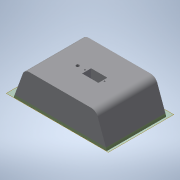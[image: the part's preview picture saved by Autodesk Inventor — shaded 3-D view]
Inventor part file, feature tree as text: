
AUTODESK INVENTOR PART (.ipt)
format: ipt  version: 2020 (Build 240168000, 168)  size: 355,328 bytes
history: native  units: mm
features: extrude x13, sketch x10, other x7, reference x6, projected_geometry x4, fillet x1, hole x1
ambient origin geometry x8: Origin, YZ Plane, XZ Plane, XY Plane, X Axis, Y Axis, Z Axis, Center Point
bodies: Body1 (feature_tree)
feature tree (42):
  other  "Bryła1"
  sketch  "Szkic1"
  other  "Płaszczyzna konstrukcyjna1"
  extrude  "Wyciągnięcie proste1"  Depth=3.0mm
  sketch  "Szkic2"
  other  "Płaszczyzna konstrukcyjna2"
  extrude  "Wyciągnięcie proste2"  Depth=3.0mm
  extrude  "Wyciągnięcie proste3"  Depth=3.0mm
  extrude  "Wyciągnięcie proste4"  Depth=40.0mm
  extrude  "Wyciągnięcie proste5"  Depth=12.217305mm
  extrude  "Wyciągnięcie proste6"  Depth=12.217305mm
  fillet  "Zaokrąglenie1"  Radius=75.0mm
  extrude  "Wyciągnięcie proste7"  Depth=3.0mm TaperAngle=0.0deg
  extrude  "Wyciągnięcie proste8"  Depth=83.0mm TaperAngle=0.0deg
  other  "Płaszczyzna konstrukcyjna3"
  extrude  "Wyciągnięcie proste9"  Depth=3.0mm TaperAngle=0.0deg
  extrude  "Wyciągnięcie proste10"  Depth=27.0mm
  sketch  "Szkic13"
  extrude  "Wyciągnięcie proste11"  Depth=20.0mm
  hole  "Otwór1"  [1 undecoded]
  extrude  "Wyciągnięcie proste12"  Depth=7.0mm
  extrude  "Wyciągnięcie proste13"  Depth=7.0mm
  reference  "Odniesienie1"
  reference  "Odniesienie2"
  reference  "Odniesienie3"
  sketch  "Szkic3"
  projected_geometry  "Pętla rzutowana1"
  sketch  "Szkic4"
  sketch  "Szkic5"
  reference  "Odniesienie4"
  reference  "Odniesienie5"
  sketch  "Szkic6"
  reference  "Odniesienie6"
  sketch  "Szkic11"
  projected_geometry  "Pętla rzutowana4"
  sketch  "Szkic12"
  projected_geometry  "Pętla rzutowana5"
  sketch  "Szkic14"
  projected_geometry  "Pętla rzutowana6"
  other  "<userpath>\Desktop\ScanBot\3d-model\Assembly1.iam"
  other  "Assembly1.iam"
  other  "base-v2:1"
note: 1 required parameter value undecoded (feature->parameter linkage not recoverable at this tier; creation-order binding heuristic only, values carry confidence <= 0.55)
